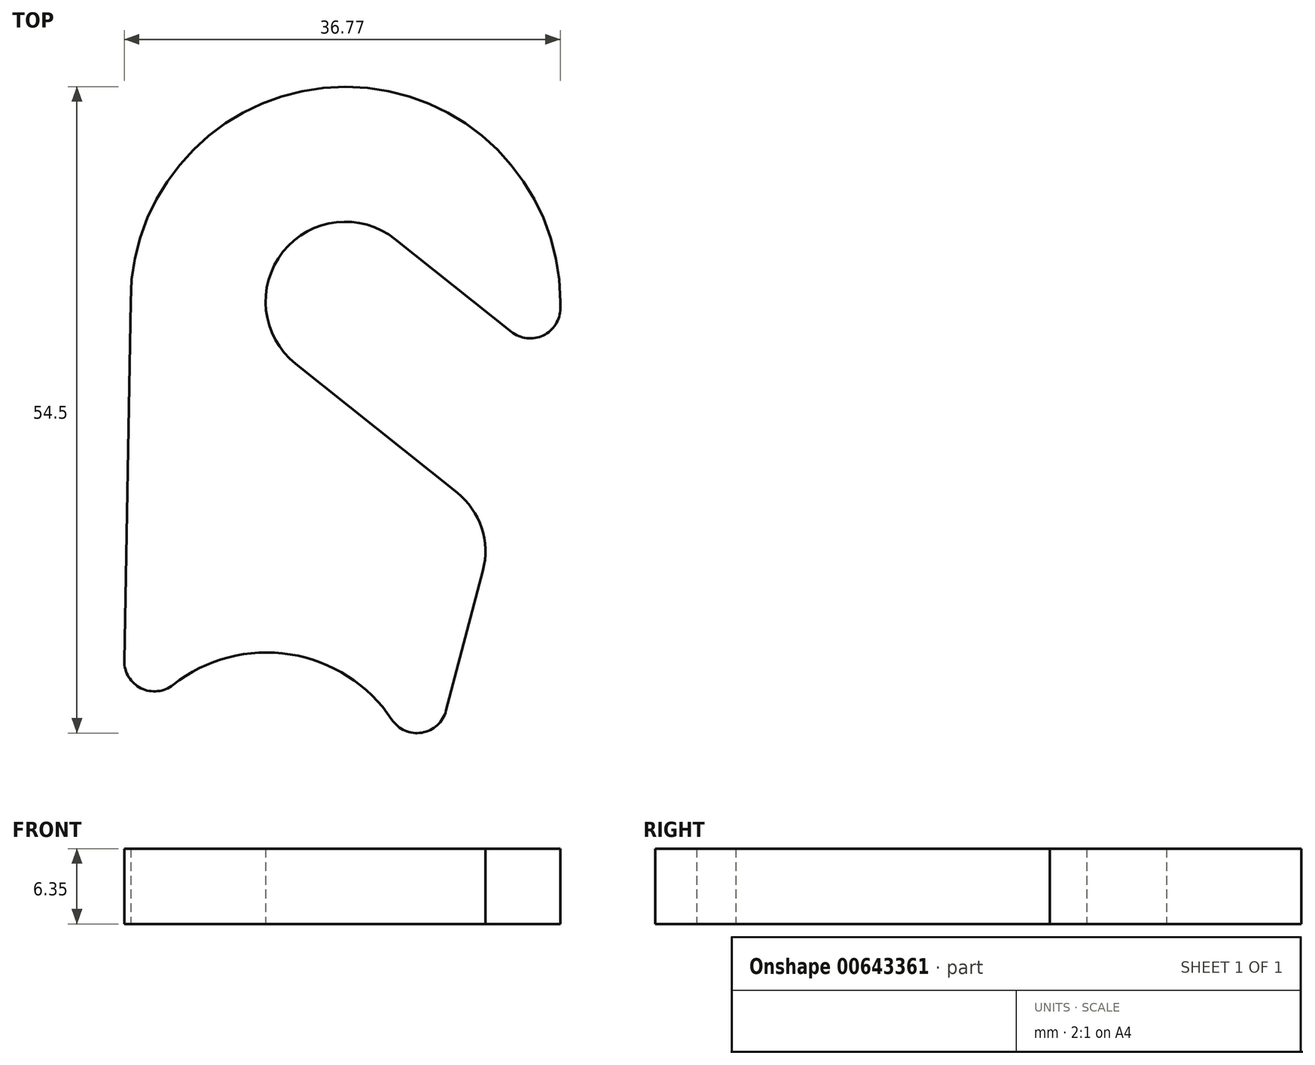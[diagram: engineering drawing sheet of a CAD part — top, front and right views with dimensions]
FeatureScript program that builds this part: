
annotation { "Feature Type Name" : "Feature", "Feature Type Description" : "" }
export const myFeature = defineFeature(function(context is Context, id is Id, definition is map)
    precondition{}
    {
        {
            var Q0;
            Q0=qCreatedBy(makeId("Top.planeOp"),FACE);
            var sketch = newSketch(context, id + "F0", { "sketchPlane" : qUnion([Q0])});
            skArc(sketch, "E0", {"start": v(-0.28, -20.91) * mm, "mid": v(-8.87, -15.4) * mm, "end": v(-18.73, -17.98) * mm});
            skArc(sketch, "E1", {"start": v(13.92, 14.34) * mm, "mid": v(-4.2, 32.46) * mm, "end": v(-22.32, 14.34) * mm});
            skArc(sketch, "E2", {"start": v(0, 19.6) * mm, "mid": v(-9.46, 18.54) * mm, "end": v(-8.4, 9.08) * mm});
            skLineSegment(sketch, "E3", {"start": v(-8.4, 9.08) * mm, "end": v(5.21, -1.78) * mm});
            skLineSegment(sketch, "E4", {"start": v(0, 19.6) * mm, "end": v(9.8, 11.79) * mm});
            skLineSegment(sketch, "E5.trimOffspring", {"start": v(13.92, 13.78) * mm, "end": v(13.92, 14.34) * mm});
            skPoint(sketch, "E6.visualSharp", {"position": v(13.92, 8.5) * mm});
            skArc(sketch, "E6.filletArc", {"start": v(9.8, 11.79) * mm, "mid": v(12.48, 11.49) * mm, "end": v(13.92, 13.78) * mm});
            skLineSegment(sketch, "E7", {"start": v(-22.32, 14.34) * mm, "end": v(-22.85, -15.94) * mm});
            skLineSegment(sketch, "E8", {"start": v(4.29, -20.15) * mm, "end": v(7.4, -8.36) * mm});
            skPoint(sketch, "E9.visualSharp", {"position": v(-22.99, -24.2) * mm});
            skArc(sketch, "E9.filletArc", {"start": v(-22.85, -15.94) * mm, "mid": v(-21.43, -18.27) * mm, "end": v(-18.73, -17.98) * mm});
            skPoint(sketch, "E10.visualSharp", {"position": v(1.12, -32.17) * mm});
            skArc(sketch, "E10.filletArc", {"start": v(-0.28, -20.91) * mm, "mid": v(2.25, -22) * mm, "end": v(4.29, -20.15) * mm});
            skPoint(sketch, "E11.visualSharp", {"position": v(8.45, -4.36) * mm});
            skArc(sketch, "E11.filletArc", {"start": v(7.4, -8.36) * mm, "mid": v(7.28, -4.74) * mm, "end": v(5.21, -1.78) * mm});
            skSolve(sketch);
        }
        {
            var Q0;
            Q0=makeQuery(id+"F0.imprint","IMPRINT",FACE,{"disambiguationData":[TD([[makeQuery(id+"F0.imprint","IMPRINT",EDGE,{"derivedFrom":sQuery(id+"F0.wireOp",EDGE,"E0")}),-1.0]])]});
            extrude(context, id + "F1", {"entities" : qUnion([Q0]), "depth" : 6.35 * mm, "offsetDistance" : 25.4 * mm});
        }
    });
